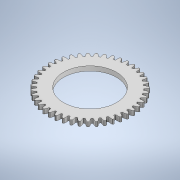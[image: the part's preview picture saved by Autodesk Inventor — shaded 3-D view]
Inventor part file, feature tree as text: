
AUTODESK INVENTOR PART (.ipt)
format: ipt  version: 2020 (Build 240168000, 168)  size: 525,824 bytes
history: native  units: mm
features: extrude x2, sketch x2, fillet x1, pattern_circular x1
ambient origin geometry x8: Origin, YZ Plane, XZ Plane, XY Plane, X Axis, Y Axis, Z Axis, Center Point
bodies: Solid1 (feature_tree)
feature tree (6):
  extrude  "Extrusion1"  Depth=3.0mm TaperAngle=360.0deg
  fillet  "Fillet2"  Radius=53.2mm
  pattern_circular  "Circular Pattern2"  [2 undecoded]
  extrude  "Extrusion3"  Depth=10.0mm
  sketch  "Sketch1"  dims[d4=3.0mm d5=0.0mm d18=430.0mm d19=360.0deg d23=53.2mm]
  sketch  "Sketch3"  dims[d25=1.546512mm d26=1.237209mm d27=3.490659mm d28=49.991647mm d29=3.490659mm d30=0.309302mm d31=0.618605mm d32=0.971704mm d33=0.4mm d34=35.0mm d35=10.0mm d36=0.0mm]
note: 2 required parameter values undecoded (feature->parameter linkage not recoverable at this tier; creation-order binding heuristic only, values carry confidence <= 0.55)
